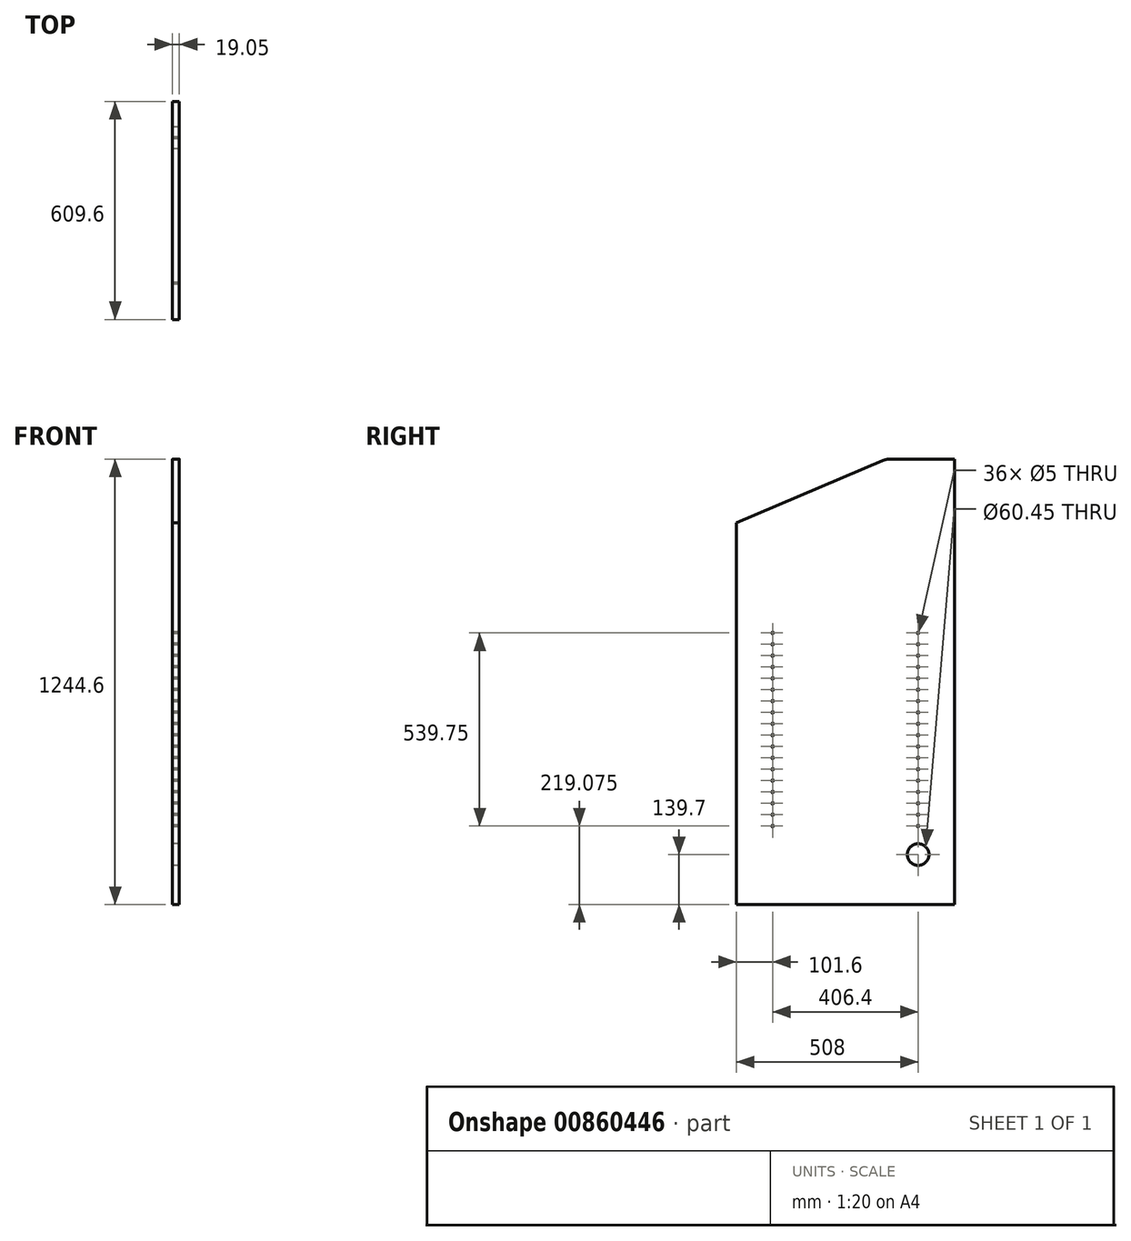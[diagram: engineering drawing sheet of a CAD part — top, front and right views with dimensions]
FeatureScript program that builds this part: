
annotation { "Feature Type Name" : "Feature", "Feature Type Description" : "" }
export const myFeature = defineFeature(function(context is Context, id is Id, definition is map)
    precondition{}
    {
        {
            var Q0;
            Q0=qCreatedBy(makeId("Right.planeOp"),FACE);
            var sketch = newSketch(context, id + "F0", { "sketchPlane" : qUnion([Q0])});
            skLineSegment(sketch, "E0.bottom", {"start": v(304.8, 622.3) * mm, "end": v(-304.8, 622.3) * mm});
            skLineSegment(sketch, "E0.top", {"start": v(304.8, -622.3) * mm, "end": v(-304.8, -622.3) * mm});
            skLineSegment(sketch, "E0.left", {"start": v(304.8, 622.3) * mm, "end": v(304.8, -622.3) * mm});
            skLineSegment(sketch, "E0.right", {"start": v(-304.8, 622.3) * mm, "end": v(-304.8, -622.3) * mm});
            skPoint(sketch, "E0.middle", {"position": v(0, 0) * mm});
            skLineSegment(sketch, "E1", {"start": v(304.8, 622.3) * mm, "end": v(124.63, 622.3) * mm});
            skLineSegment(sketch, "E2", {"start": v(-304.8, 622.3) * mm, "end": v(-304.8, 444.5) * mm});
            skLineSegment(sketch, "E3", {"start": v(-304.8, 444.5) * mm, "end": v(104.8, 618.27) * mm});
            skPoint(sketch, "E4.visualSharp", {"position": v(114.3, 622.3) * mm});
            skArc(sketch, "E4.filletArc", {"start": v(124.63, 622.3) * mm, "mid": v(114.5, 621.28) * mm, "end": v(104.8, 618.27) * mm});
            skLineSegment(sketch, "E5", {"start": v(-304.8, 444.5) * mm, "end": v(-304.8, 396.87) * mm});
            skCircle(sketch, "E6", {"center": v(203.2, -482.6) * mm, "radius": 30.23 * mm});
            skLineSegment(sketch, "E7", {"start": v(203.2, -482.6) * mm, "end": v(304.8, -482.6) * mm});
            skLineSegment(sketch, "E8", {"start": v(304.8, -482.6) * mm, "end": v(304.8, -622.3) * mm});
            skSolve(sketch);
        }
        {
            var Q0;
            Q0=makeQuery(id+"F0.imprint","IMPRINT",FACE,{"disambiguationData":[TD([[makeQuery(id+"F0.imprint","IMPRINT",EDGE,{"derivedFrom":sQuery(id+"F0.wireOp",EDGE,"E0.top")}),-1.0]])]});
            extrude(context, id + "F1", {"entities" : qUnion([Q0]), "depth" : 19.05 * mm, "offsetDistance" : 25.4 * mm});
        }
        {
            var Q0;
            Q0=makeQuery(id+"F1.opExtrude","CAP_FACE",FACE,{"disambiguationData":[OSD([sQuery(id+"F0.wireOp",EDGE,"E0.top"),sQuery(id+"F0.wireOp",EDGE,"E0.left"),sQuery(id+"F0.wireOp",EDGE,"E0.right"),sQuery(id+"F0.wireOp",EDGE,"E1"),sQuery(id+"F0.wireOp",EDGE,"E3"),sQuery(id+"F0.wireOp",EDGE,"E4.filletArc"),sQuery(id+"F0.wireOp",EDGE,"E5")])],"isStart":false});
            var sketch = newSketch(context, id + "F2", { "sketchPlane" : qUnion([Q0])});
            skLineSegment(sketch, "E9", {"start": v(0, -622.3) * mm, "end": v(0, -387.35) * mm});
            skLineSegment(sketch, "E10.bottom", {"start": v(203.2, -371.48) * mm, "end": v(-203.2, -371.48) * mm});
            skLineSegment(sketch, "E10.top", {"start": v(203.2, -403.23) * mm, "end": v(-203.2, -403.23) * mm});
            skLineSegment(sketch, "E10.left", {"start": v(203.2, -371.48) * mm, "end": v(203.2, -403.23) * mm});
            skLineSegment(sketch, "E10.right", {"start": v(-203.2, -371.48) * mm, "end": v(-203.2, -403.23) * mm});
            skPoint(sketch, "E10.middle", {"position": v(0, -387.35) * mm});
            skLineSegment(sketch, "E11.bottom", {"start": v(203.2, -339.73) * mm, "end": v(-203.2, -339.73) * mm});
            skLineSegment(sketch, "E11.top", {"start": v(203.2, -307.98) * mm, "end": v(-203.2, -307.98) * mm});
            skLineSegment(sketch, "E11.left", {"start": v(203.2, -339.73) * mm, "end": v(203.2, -307.98) * mm});
            skLineSegment(sketch, "E11.right", {"start": v(-203.2, -339.73) * mm, "end": v(-203.2, -307.98) * mm});
            skPoint(sketch, "E11.middle", {"position": v(0, -323.85) * mm});
            skLineSegment(sketch, "E12", {"start": v(0, -323.85) * mm, "end": v(0, -260.35) * mm});
            skLineSegment(sketch, "E13.bottom", {"start": v(203.2, -276.23) * mm, "end": v(-203.2, -276.23) * mm});
            skLineSegment(sketch, "E13.top", {"start": v(203.2, -244.48) * mm, "end": v(-203.2, -244.48) * mm});
            skLineSegment(sketch, "E13.left", {"start": v(203.2, -276.23) * mm, "end": v(203.2, -244.48) * mm});
            skLineSegment(sketch, "E13.right", {"start": v(-203.2, -276.23) * mm, "end": v(-203.2, -244.48) * mm});
            skPoint(sketch, "E13.middle", {"position": v(0, -260.35) * mm});
            skLineSegment(sketch, "E14", {"start": v(0, -260.35) * mm, "end": v(0, -196.85) * mm});
            skLineSegment(sketch, "E15.bottom", {"start": v(-203.2, -212.73) * mm, "end": v(203.2, -212.73) * mm});
            skLineSegment(sketch, "E15.top", {"start": v(-203.2, -180.98) * mm, "end": v(203.2, -180.98) * mm});
            skLineSegment(sketch, "E15.left", {"start": v(-203.2, -212.73) * mm, "end": v(-203.2, -180.98) * mm});
            skLineSegment(sketch, "E15.right", {"start": v(203.2, -212.73) * mm, "end": v(203.2, -180.98) * mm});
            skPoint(sketch, "E15.middle", {"position": v(0, -196.85) * mm});
            skLineSegment(sketch, "E16", {"start": v(0, -196.85) * mm, "end": v(0, -133.35) * mm});
            skLineSegment(sketch, "E17.bottom", {"start": v(-203.2, -149.23) * mm, "end": v(203.2, -149.23) * mm});
            skLineSegment(sketch, "E17.top", {"start": v(-203.2, -117.48) * mm, "end": v(203.2, -117.48) * mm});
            skLineSegment(sketch, "E17.left", {"start": v(-203.2, -149.23) * mm, "end": v(-203.2, -117.48) * mm});
            skLineSegment(sketch, "E17.right", {"start": v(203.2, -149.23) * mm, "end": v(203.2, -117.48) * mm});
            skPoint(sketch, "E17.middle", {"position": v(0, -133.35) * mm});
            skLineSegment(sketch, "E18", {"start": v(0, -133.35) * mm, "end": v(0, -69.85) * mm});
            skLineSegment(sketch, "E19.bottom", {"start": v(-203.2, -85.73) * mm, "end": v(203.2, -85.73) * mm});
            skLineSegment(sketch, "E19.top", {"start": v(-203.2, -53.98) * mm, "end": v(203.2, -53.98) * mm});
            skLineSegment(sketch, "E19.left", {"start": v(-203.2, -85.73) * mm, "end": v(-203.2, -53.98) * mm});
            skLineSegment(sketch, "E19.right", {"start": v(203.2, -85.73) * mm, "end": v(203.2, -53.98) * mm});
            skPoint(sketch, "E19.middle", {"position": v(0, -69.85) * mm});
            skLineSegment(sketch, "E20", {"start": v(0, -69.85) * mm, "end": v(0, -6.35) * mm});
            skLineSegment(sketch, "E21.bottom", {"start": v(-203.2, -22.23) * mm, "end": v(203.2, -22.23) * mm});
            skLineSegment(sketch, "E21.top", {"start": v(-203.2, 9.52) * mm, "end": v(203.2, 9.52) * mm});
            skLineSegment(sketch, "E21.left", {"start": v(-203.2, -22.23) * mm, "end": v(-203.2, 9.52) * mm});
            skLineSegment(sketch, "E21.right", {"start": v(203.2, -22.23) * mm, "end": v(203.2, 9.52) * mm});
            skPoint(sketch, "E21.middle", {"position": v(0, -6.35) * mm});
            skLineSegment(sketch, "E22", {"start": v(0, -6.35) * mm, "end": v(0, 57.15) * mm});
            skLineSegment(sketch, "E23.bottom", {"start": v(-203.2, 73.02) * mm, "end": v(203.2, 73.02) * mm});
            skLineSegment(sketch, "E23.top", {"start": v(-203.2, 41.27) * mm, "end": v(203.2, 41.27) * mm});
            skLineSegment(sketch, "E23.left", {"start": v(-203.2, 73.02) * mm, "end": v(-203.2, 41.27) * mm});
            skLineSegment(sketch, "E23.right", {"start": v(203.2, 73.02) * mm, "end": v(203.2, 41.27) * mm});
            skPoint(sketch, "E23.middle", {"position": v(0, 57.15) * mm});
            skLineSegment(sketch, "E24", {"start": v(0, 57.15) * mm, "end": v(0, 120.65) * mm});
            skLineSegment(sketch, "E25.bottom", {"start": v(-203.2, 104.77) * mm, "end": v(203.2, 104.77) * mm});
            skLineSegment(sketch, "E25.top", {"start": v(-203.2, 136.52) * mm, "end": v(203.2, 136.52) * mm});
            skLineSegment(sketch, "E25.left", {"start": v(-203.2, 104.77) * mm, "end": v(-203.2, 136.52) * mm});
            skLineSegment(sketch, "E25.right", {"start": v(203.2, 104.77) * mm, "end": v(203.2, 136.52) * mm});
            skPoint(sketch, "E25.middle", {"position": v(0, 120.65) * mm});
            skSolve(sketch);
        }
        {
            var Q0;
            Q0=sQuery(id+"F2.wireOp",VERTEX,"E25.top.start");
            var Q1;
            Q1=sQuery(id+"F2.wireOp",VERTEX,"E25.bottom.start");
            var Q2;
            Q2=sQuery(id+"F2.wireOp",VERTEX,"E23.bottom.start");
            var Q3;
            Q3=sQuery(id+"F2.wireOp",VERTEX,"E23.top.start");
            var Q4;
            Q4=sQuery(id+"F2.wireOp",VERTEX,"E21.top.start");
            var Q5;
            Q5=sQuery(id+"F2.wireOp",VERTEX,"E21.bottom.start");
            var Q6;
            Q6=sQuery(id+"F2.wireOp",VERTEX,"E19.top.start");
            var Q7;
            Q7=sQuery(id+"F2.wireOp",VERTEX,"E19.bottom.start");
            var Q8;
            Q8=sQuery(id+"F2.wireOp",VERTEX,"E17.top.start");
            var Q9;
            Q9=sQuery(id+"F2.wireOp",VERTEX,"E17.bottom.start");
            var Q10;
            Q10=sQuery(id+"F2.wireOp",VERTEX,"E15.top.start");
            var Q11;
            Q11=sQuery(id+"F2.wireOp",VERTEX,"E15.bottom.start");
            var Q12;
            Q12=sQuery(id+"F2.wireOp",VERTEX,"E13.top.end");
            var Q13;
            Q13=sQuery(id+"F2.wireOp",VERTEX,"E13.bottom.end");
            var Q14;
            Q14=sQuery(id+"F2.wireOp",VERTEX,"E11.top.end");
            var Q15;
            Q15=sQuery(id+"F2.wireOp",VERTEX,"E11.bottom.end");
            var Q16;
            Q16=sQuery(id+"F2.wireOp",VERTEX,"E10.bottom.end");
            var Q17;
            Q17=sQuery(id+"F2.wireOp",VERTEX,"E10.top.end");
            var Q18;
            Q18=sQuery(id+"F2.wireOp",VERTEX,"E10.top.start");
            var Q19;
            Q19=sQuery(id+"F2.wireOp",VERTEX,"E10.bottom.start");
            var Q20;
            Q20=sQuery(id+"F2.wireOp",VERTEX,"E11.bottom.start");
            var Q21;
            Q21=sQuery(id+"F2.wireOp",VERTEX,"E11.top.start");
            var Q22;
            Q22=sQuery(id+"F2.wireOp",VERTEX,"E13.bottom.start");
            var Q23;
            Q23=sQuery(id+"F2.wireOp",VERTEX,"E13.top.start");
            var Q24;
            Q24=sQuery(id+"F2.wireOp",VERTEX,"E15.bottom.end");
            var Q25;
            Q25=sQuery(id+"F2.wireOp",VERTEX,"E15.top.end");
            var Q26;
            Q26=sQuery(id+"F2.wireOp",VERTEX,"E17.bottom.end");
            var Q27;
            Q27=sQuery(id+"F2.wireOp",VERTEX,"E17.top.end");
            var Q28;
            Q28=sQuery(id+"F2.wireOp",VERTEX,"E19.bottom.end");
            var Q29;
            Q29=sQuery(id+"F2.wireOp",VERTEX,"E19.top.end");
            var Q30;
            Q30=sQuery(id+"F2.wireOp",VERTEX,"E21.bottom.end");
            var Q31;
            Q31=sQuery(id+"F2.wireOp",VERTEX,"E21.top.end");
            var Q32;
            Q32=sQuery(id+"F2.wireOp",VERTEX,"E23.top.end");
            var Q33;
            Q33=sQuery(id+"F2.wireOp",VERTEX,"E23.bottom.end");
            var Q34;
            Q34=sQuery(id+"F2.wireOp",VERTEX,"E25.bottom.end");
            var Q35;
            Q35=sQuery(id+"F2.wireOp",VERTEX,"E25.top.end");
            var Q36;
            Q36=makeQuery(id+"F1.opExtrude","SWEPT_BODY",BODY,{"disambiguationData":[OSD([sQuery(id+"F0.wireOp",EDGE,"E0.top"),sQuery(id+"F0.wireOp",EDGE,"E0.left"),sQuery(id+"F0.wireOp",EDGE,"E0.right"),sQuery(id+"F0.wireOp",EDGE,"E1"),sQuery(id+"F0.wireOp",EDGE,"E3"),sQuery(id+"F0.wireOp",EDGE,"E4.filletArc"),sQuery(id+"F0.wireOp",EDGE,"E5")])]});
            hole(context, id + "F3", {"style" : HoleStyle.SIMPLE, "endStyle" : HoleEndStyle.BLIND, "holeDiameter" : 5 * mm, "majorDiameter" : 6.35 * mm, "holeDepth" : 14.22 * mm, "isTappedThrough" : true, "tappedDepth" : 12.7 * mm, "tapClearance" : 3, "locations" : qUnion([Q0, Q1, Q2, Q3, Q4, Q5, Q6, Q7, Q8, Q9, Q10, Q11, Q12, Q13, Q14, Q15, Q16, Q17, Q18, Q19, Q20, Q21, Q22, Q23, Q24, Q25, Q26, Q27, Q28, Q29, Q30, Q31, Q32, Q33, Q34, Q35]), "scope" : qUnion([Q36]), "startStyle" : HoleStartStyle.SKETCH});
        }
    });
